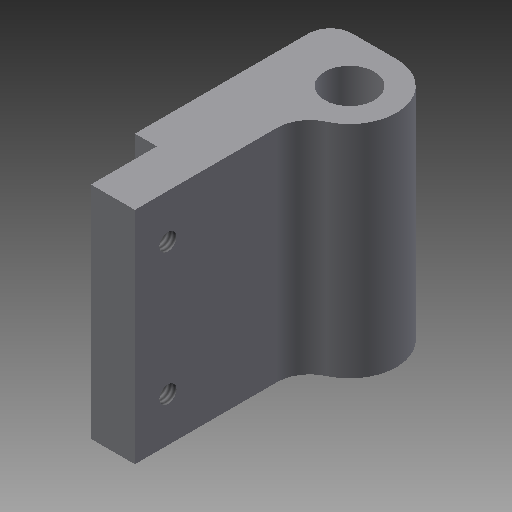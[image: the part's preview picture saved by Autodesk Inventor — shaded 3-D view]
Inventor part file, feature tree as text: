
AUTODESK INVENTOR PART (.ipt)
format: ipt  version: 2018 (Build 220112000, 112)  size: 123,392 bytes
history: native  units: mm
features: hole x2, fillet x2, sketch x2, extrude x1
ambient origin geometry x8: Origin, YZ Plane, XZ Plane, XY Plane, X Axis, Y Axis, Z Axis, Center Point
bodies: Volumenkörper1 (feature_tree)
feature tree (7):
  extrude  "Extrusion1"  Depth=4.0mm
  hole  "Bohrung1"  [1 undecoded]
  hole  "Bohrung2"  [1 undecoded]
  fillet  "Rundung1"  Radius=6.0mm
  fillet  "Rundung2"  Radius=20.0mm
  sketch  "Skizze2"  dims[d0=4.5mm d1=4.0mm]
  sketch  "Skizze3"  dims[d2=2.0mm d3=2.0mm d4=13.5mm d5=6.0mm d6=20.0mm d7=0.0mm d8=4.0mm d9=4.0mm d10=1.567mm d11=6.0mm d12=4.0mm d13=2.0mm d14=90.0deg d15=8.0mm d16=20.594885mm d17=4.0mm d18=4.0mm d19=1.567mm d20=6.0mm d21=4.0mm d22=2.0mm d23=90.0deg d24=8.0mm d25=20.594885mm d26=2.0mm d27=3.0mm]
note: 2 required parameter values undecoded (feature->parameter linkage not recoverable at this tier; creation-order binding heuristic only, values carry confidence <= 0.55)
